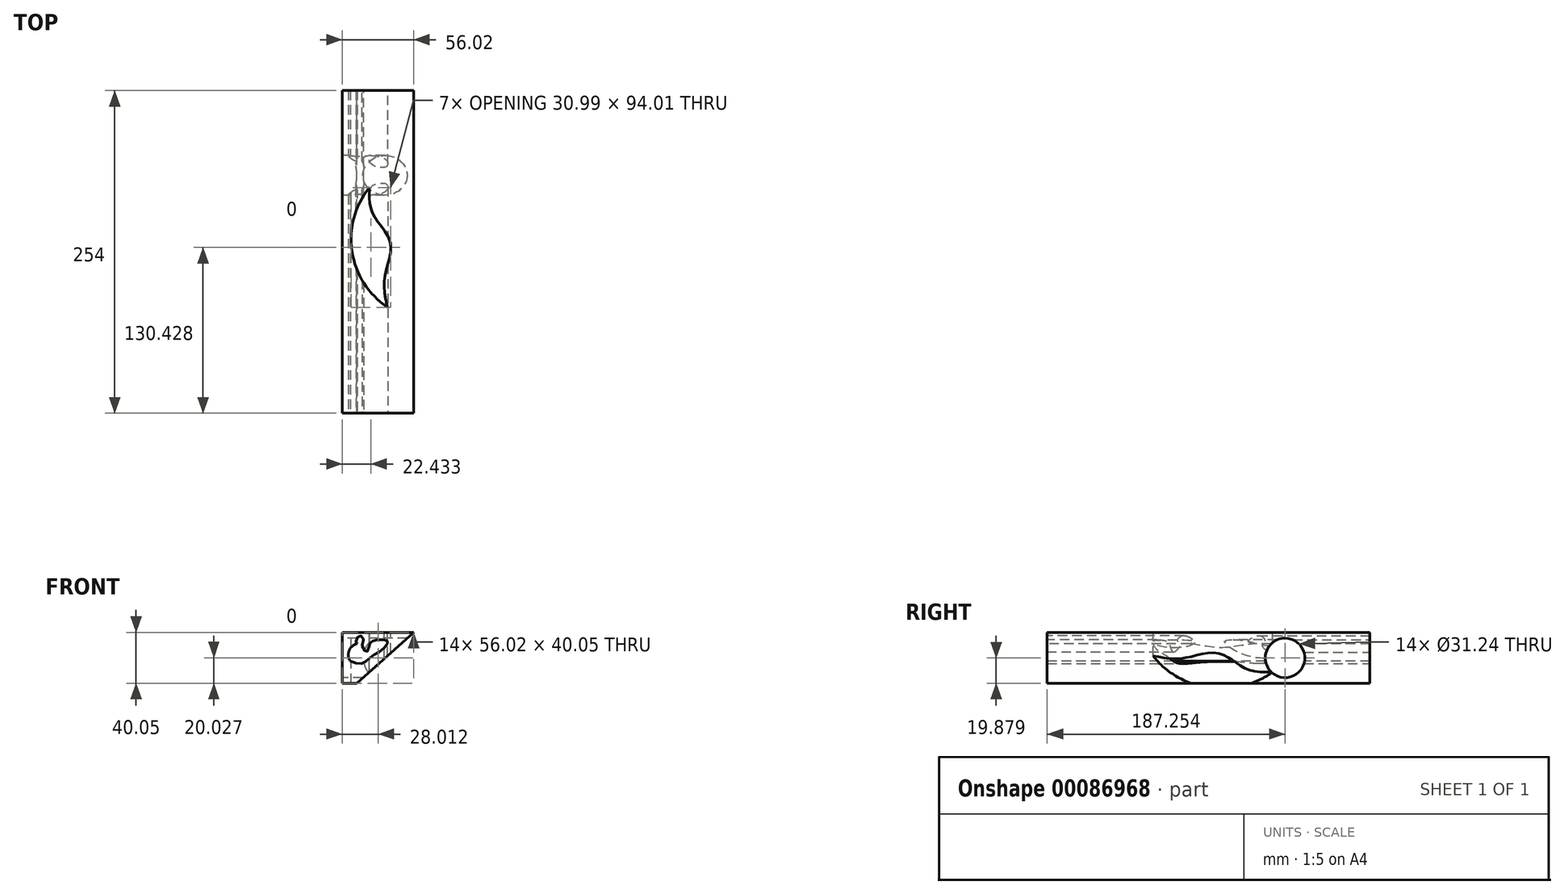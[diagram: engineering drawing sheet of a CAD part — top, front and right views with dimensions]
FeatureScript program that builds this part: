
annotation { "Feature Type Name" : "Feature", "Feature Type Description" : "" }
export const myFeature = defineFeature(function(context is Context, id is Id, definition is map)
    precondition{}
    {
        {
            var Q0;
            Q0=qCreatedBy(makeId("Front.planeOp"),FACE);
            var sketch = newSketch(context, id + "F0", { "sketchPlane" : qUnion([Q0])});
            skLineSegment(sketch, "E0", {"start": v(-56.02, 0) * mm, "end": v(-56.02, 40.05) * mm});
            skLineSegment(sketch, "E1", {"start": v(-56.02, 40.05) * mm, "end": v(0, 40.05) * mm});
            skLineSegment(sketch, "E2", {"start": v(0, 40.05) * mm, "end": v(-44.66, 0) * mm});
            skLineSegment(sketch, "E3", {"start": v(-44.66, 0) * mm, "end": v(-56.02, 0) * mm});
            skSolve(sketch);
        }
        {
            var Q0;
            Q0 = qSketchRegion(id + "F0", true);
            extrude(context, id + "F1", {"entities" : qUnion([Q0]), "endBound" : BoundingType.SYMMETRIC, "depth" : 254 * mm});
        }
        {
            var Q0;
            Q0=makeQuery(id+"F1.opExtrude","SWEPT_FACE",FACE,{"disambiguationData":[OSD([sQuery(id+"F0.wireOp",EDGE,"E1")])]});
            var sketch = newSketch(context, id + "F2", { "sketchPlane" : qUnion([Q0])});
            skArc(sketch, "E4", {"start": v(-34.93, 50.43) * mm, "mid": v(-48.44, 0.27) * mm, "end": v(-20.57, -43.58) * mm});
            skFitSpline(sketch, "E5", {"points": [v(-34.93, 50.43) * mm, v(-31.66, 29.22) * mm, v(-18.28, 7.34) * mm, v(-22.85, -20.73) * mm, v(-20.57, -43.58) * mm], "startDerivative": vector(-1, -93.53) * mm, "endDerivative": vector(21.74, -90.61) * mm});
            skSolve(sketch);
        }
        {
            var Q0;
            Q0 = qSketchRegion(id + "F2", true);
            extrude(context, id + "F3", {"entities" : qUnion([Q0]), "operationType" : NewBodyOperationType.REMOVE, "oppositeDirection" : true, "depth" : 57.12 * mm});
        }
        {
            var Q0;
            Q0=makeQuery(id+"F1.opExtrude","CAP_FACE",FACE,{"disambiguationData":[OSD([sQuery(id+"F0.wireOp",EDGE,"E0"),sQuery(id+"F0.wireOp",EDGE,"E1"),sQuery(id+"F0.wireOp",EDGE,"E2"),sQuery(id+"F0.wireOp",EDGE,"E3")])],"isStart":false});
            var sketch = newSketch(context, id + "F4", { "sketchPlane" : qUnion([Q0])});
            skArc(sketch, "E6", {"start": v(-44.46, 31.1) * mm, "mid": v(-50.73, 25.68) * mm, "end": v(-49.9, 17.43) * mm});
            skFitSpline(sketch, "E7", {"points": [v(-49.9, 17.43) * mm, v(-40.01, 15.62) * mm, v(-33.6, 20.72) * mm, v(-24.04, 26.98) * mm, v(-20.41, 33.08) * mm, v(-26.18, 34.23) * mm, v(-32.6, 33.08) * mm, v(-35.07, 29.45) * mm, v(-37.05, 24.51) * mm, v(-40.67, 30.77) * mm, v(-39.2, 33.4) * mm, v(-42.15, 37.52) * mm, v(-45.45, 33.08) * mm, v(-44.46, 31.1) * mm], "startDerivative": vector(109.1, -39.73) * mm, "endDerivative": vector(33.9, -31.38) * mm});
            skSolve(sketch);
        }
        {
            var Q0;
            Q0 = qSketchRegion(id + "F4", true);
            extrude(context, id + "F5", {"entities" : qUnion([Q0]), "operationType" : NewBodyOperationType.REMOVE, "oppositeDirection" : true, "depth" : 313.5 * mm});
        }
        {
            var Q0;
            Q0=makeQuery(id+"F1.opExtrude","SWEPT_FACE",FACE,{"disambiguationData":[OSD([sQuery(id+"F0.wireOp",EDGE,"E0")])]});
            var sketch = newSketch(context, id + "F6", { "sketchPlane" : qUnion([Q0])});
            skCircle(sketch, "E8", {"center": v(-60.25, 19.88) * mm, "radius": 15.62 * mm});
            skSolve(sketch);
        }
        {
            var Q0;
            Q0 = qSketchRegion(id + "F6", true);
            extrude(context, id + "F7", {"entities" : qUnion([Q0]), "operationType" : NewBodyOperationType.REMOVE, "oppositeDirection" : true, "depth" : 77.48 * mm});
        }
    });
